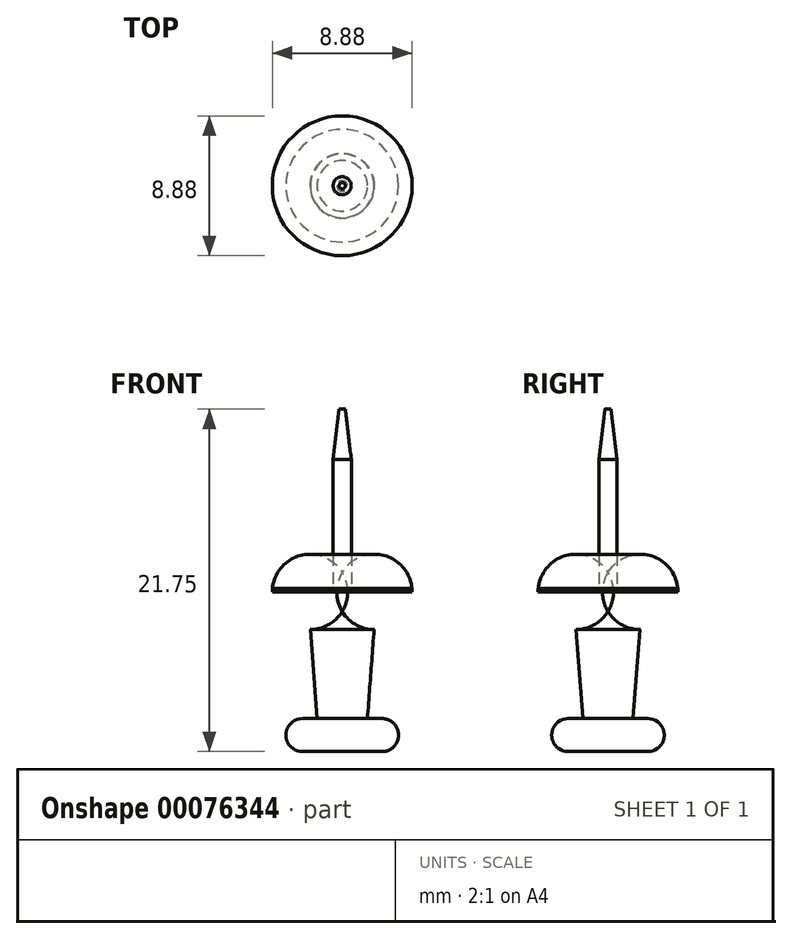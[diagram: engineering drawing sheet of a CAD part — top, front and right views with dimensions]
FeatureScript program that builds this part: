
annotation { "Feature Type Name" : "Feature", "Feature Type Description" : "" }
export const myFeature = defineFeature(function(context is Context, id is Id, definition is map)
    precondition{}
    {
        {
            var Q0;
            Q0=qCreatedBy(makeId("Top.planeOp"),FACE);
            var sketch = newSketch(context, id + "F0", { "sketchPlane" : qUnion([Q0])});
            skCircle(sketch, "E0", {"center": v(0, 0) * mm, "radius": 3.58 * mm});
            skSolve(sketch);
        }
        {
            var Q0;
            Q0=makeQuery(id+"F0.imprint","IMPRINT",FACE,{"disambiguationData":[TD([[makeQuery(id+"F0.imprint","IMPRINT",EDGE,{"derivedFrom":sQuery(id+"F0.wireOp",EDGE,"E0")}),1.0]])]});
            extrude(context, id + "F1", {"entities" : qUnion([Q0]), "depth" : 2.1 * mm});
        }
        {
            var Q0;
            Q0=makeQuery(id+"F1.opExtrude","CAP_FACE",FACE,{"disambiguationData":[OSD([sQuery(id+"F0.wireOp",EDGE,"E0")])],"isStart":false});
            var sketch = newSketch(context, id + "F2", { "sketchPlane" : qUnion([Q0])});
            skCircle(sketch, "E1", {"center": v(0, 0) * mm, "radius": 1.6 * mm});
            skSolve(sketch);
        }
        {
            var Q0;
            Q0 = qSketchRegion(id + "F2", true);
            extrude(context, id + "F3", {"entities" : qUnion([Q0]), "operationType" : NewBodyOperationType.ADD, "depth" : 8.25 * mm});
        }
        {
            var Q0;
            Q0=makeQuery(id+"F3.opExtrude","CAP_FACE",FACE,{"disambiguationData":[OSD([sQuery(id+"F2.wireOp",EDGE,"E1")])],"isStart":false});
            var sketch = newSketch(context, id + "F4", { "sketchPlane" : qUnion([Q0])});
            skCircle(sketch, "E2", {"center": v(0, 0) * mm, "radius": 4.44 * mm});
            skSolve(sketch);
        }
        {
            var Q0;
            Q0=makeQuery(id+"F4.imprint","IMPRINT",FACE,{"disambiguationData":[TD([[makeQuery(id+"F4.imprint","IMPRINT",EDGE,{"derivedFrom":sQuery(id+"F4.wireOp",EDGE,"E2")}),1.0]])]});
            extrude(context, id + "F5", {"entities" : qUnion([Q0]), "operationType" : NewBodyOperationType.ADD, "oppositeDirection" : true, "depth" : 2.6 * mm});
        }
        {
            var Q0;
            Q0=makeQuery(id+"F1.opExtrude","CAP_EDGE",EDGE,{"disambiguationData":[OSD([sQuery(id+"F0.wireOp",EDGE,"E0")])],"isStart":false});
            var Q1;
            Q1=makeQuery(id+"F1.opExtrude","CAP_EDGE",EDGE,{"disambiguationData":[OSD([sQuery(id+"F0.wireOp",EDGE,"E0")])],"isStart":true});
            fillet(context, id + "F6", {"entities" : qUnion([Q0, Q1]), "radius" : 1.05 * mm, "tangentPropagation" : true, "allowEdgeOverflow" : false});
        }
        {
            var Q0;
            Q0=makeQuery(id+"F5.opExtrude","CAP_EDGE",EDGE,{"disambiguationData":[OSD([sQuery(id+"F4.wireOp",EDGE,"E2")])],"isStart":false});
            fillet(context, id + "F7", {"entities" : qUnion([Q0]), "radius" : 2.4 * mm, "tangentPropagation" : true, "allowEdgeOverflow" : false});
        }
        {
            var Q0;
            Q0=makeQuery(id+"F5.opExtrude","CAP_FACE",FACE,{"disambiguationData":[OSD([sQuery(id+"F2.wireOp",EDGE,"E1"),sQuery(id+"F4.wireOp",EDGE,"E2")])],"isStart":false});
            var sketch = newSketch(context, id + "F8", { "sketchPlane" : qUnion([Q0])});
            skCircle(sketch, "E3", {"center": v(0, 0) * mm, "radius": 2.02 * mm});
            skSolve(sketch);
        }
        {
            var Q1;
            Q1 = qSketchRegion(id + "F2", true);
            var Q2;
            Q2 = qSketchRegion(id + "F8", true);
            loft(context, id + "F9", {"operationType" : NewBodyOperationType.ADD, "sheetProfilesArray" : [{ "sheetProfileEntities" : qUnion([Q1]) }, { "sheetProfileEntities" : qUnion([Q2]) }]});
        }
        {
            var Q0;
            {var subQ0=sQuery(id+"F2.wireOp",EDGE,"E1");Q0=makeQuery(id+"F5.boolean.opBoolean","MERGE",FACE,{"derivedFrom":[makeQuery(id+"F3.opExtrude","CAP_FACE",FACE,{"disambiguationData":[OSD([subQ0])],"isStart":false}),makeQuery(id+"F5.opExtrude","CAP_FACE",FACE,{"disambiguationData":[OSD([subQ0,sQuery(id+"F4.wireOp",EDGE,"E2")])],"isStart":true})]});}
            var sketch = newSketch(context, id + "F10", { "sketchPlane" : qUnion([Q0])});
            skCircle(sketch, "E4", {"center": v(0, 0) * mm, "radius": 0.57 * mm});
            skSolve(sketch);
        }
        {
            var Q0;
            Q0 = qSketchRegion(id + "F10", true);
            extrude(context, id + "F11", {"entities" : qUnion([Q0]), "operationType" : NewBodyOperationType.ADD, "depth" : 8.2 * mm});
        }
        {
            var Q0;
            Q0=makeQuery(id+"F11.opExtrude","CAP_FACE",FACE,{"disambiguationData":[OSD([sQuery(id+"F10.wireOp",EDGE,"E4")])],"isStart":false});
            var sketch = newSketch(context, id + "F12", { "sketchPlane" : qUnion([Q0])});
            skCircle(sketch, "E5", {"center": v(0, 0) * mm, "radius": 0.2 * mm});
            skSolve(sketch);
        }
        {
            var Q0;
            Q0 = qSketchRegion(id + "F12", true);
            extrude(context, id + "F13", {"entities" : qUnion([Q0]), "operationType" : NewBodyOperationType.ADD, "depth" : 3.2 * mm});
        }
        {
            var Q0;
            Q0=makeQuery(id+"F11.opExtrude","CAP_FACE",FACE,{"disambiguationData":[OSD([sQuery(id+"F10.wireOp",EDGE,"E4")])],"isStart":false});
            var sketch = newSketch(context, id + "F14", { "sketchPlane" : qUnion([Q0])});
            skCircle(sketch, "E6", {"center": v(0, 0) * mm, "radius": 0.57 * mm});
            skSolve(sketch);
        }
        {
            var Q0;
            Q0=makeQuery(id+"F13.opExtrude","CAP_FACE",FACE,{"disambiguationData":[OSD([sQuery(id+"F12.wireOp",EDGE,"E5")])],"isStart":false});
            var sketch = newSketch(context, id + "F15", { "sketchPlane" : qUnion([Q0])});
            skCircle(sketch, "E7", {"center": v(0, 0) * mm, "radius": 0.2 * mm});
            skSolve(sketch);
        }
        {
            var Q1;
            Q1 = qSketchRegion(id + "F14", true);
            var Q2;
            Q2 = qSketchRegion(id + "F15", true);
            loft(context, id + "F16", {"operationType" : NewBodyOperationType.ADD, "sheetProfilesArray" : [{ "sheetProfileEntities" : qUnion([Q1]) }, { "sheetProfileEntities" : qUnion([Q2]) }]});
        }
    });
